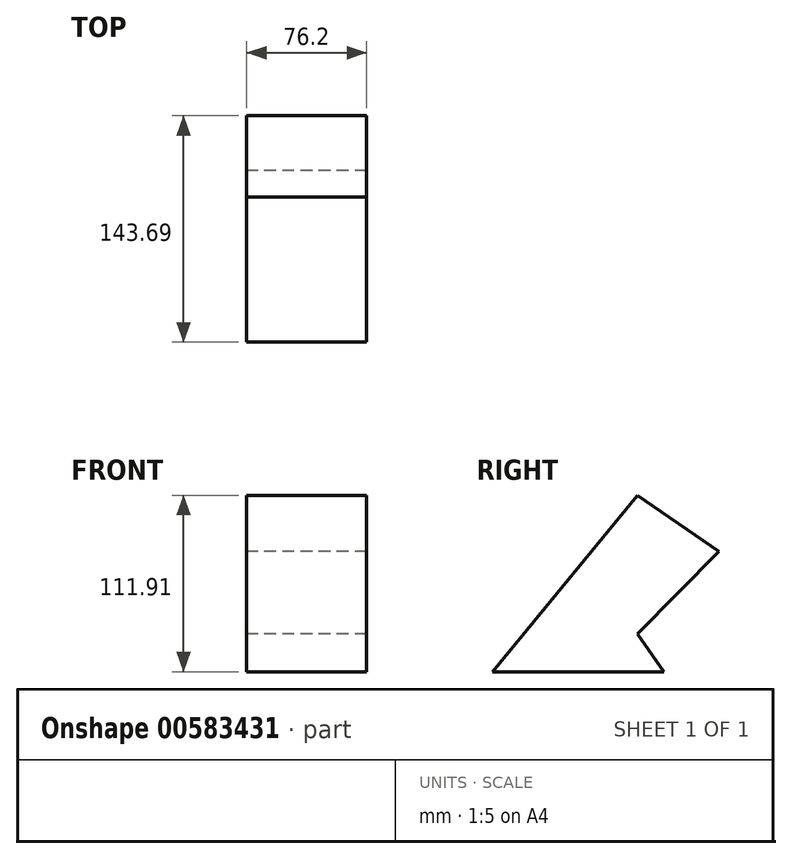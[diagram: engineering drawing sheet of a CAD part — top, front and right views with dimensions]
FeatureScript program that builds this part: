
annotation { "Feature Type Name" : "Feature", "Feature Type Description" : "" }
export const myFeature = defineFeature(function(context is Context, id is Id, definition is map)
    precondition{}
    {
        {
            var Q0;
            Q0=qCreatedBy(makeId("Right.planeOp"),FACE);
            var sketch = newSketch(context, id + "F0", { "sketchPlane" : qUnion([Q0])});
            skLineSegment(sketch, "E0", {"start": v(-60.29, 0) * mm, "end": v(31.67, 111.9) * mm});
            skLineSegment(sketch, "E1", {"start": v(31.67, 111.9) * mm, "end": v(83.4, 76.35) * mm});
            skLineSegment(sketch, "E2", {"start": v(83.4, 76.35) * mm, "end": v(31.67, 23.9) * mm});
            skLineSegment(sketch, "E3", {"start": v(31.67, 23.9) * mm, "end": v(48.55, 0) * mm});
            skLineSegment(sketch, "E4", {"start": v(48.55, 0) * mm, "end": v(-60.29, 0) * mm});
            skSolve(sketch);
        }
        {
            var Q0;
            Q0=makeQuery(id+"F0.imprint","IMPRINT",FACE,{"disambiguationData":[TD([[makeQuery(id+"F0.imprint","IMPRINT",EDGE,{"derivedFrom":sQuery(id+"F0.wireOp",EDGE,"E0")}),-1.0]])]});
            extrude(context, id + "F1", {"entities" : qUnion([Q0]), "depth" : 76.2 * mm, "offsetDistance" : 25.4 * mm});
        }
    });
